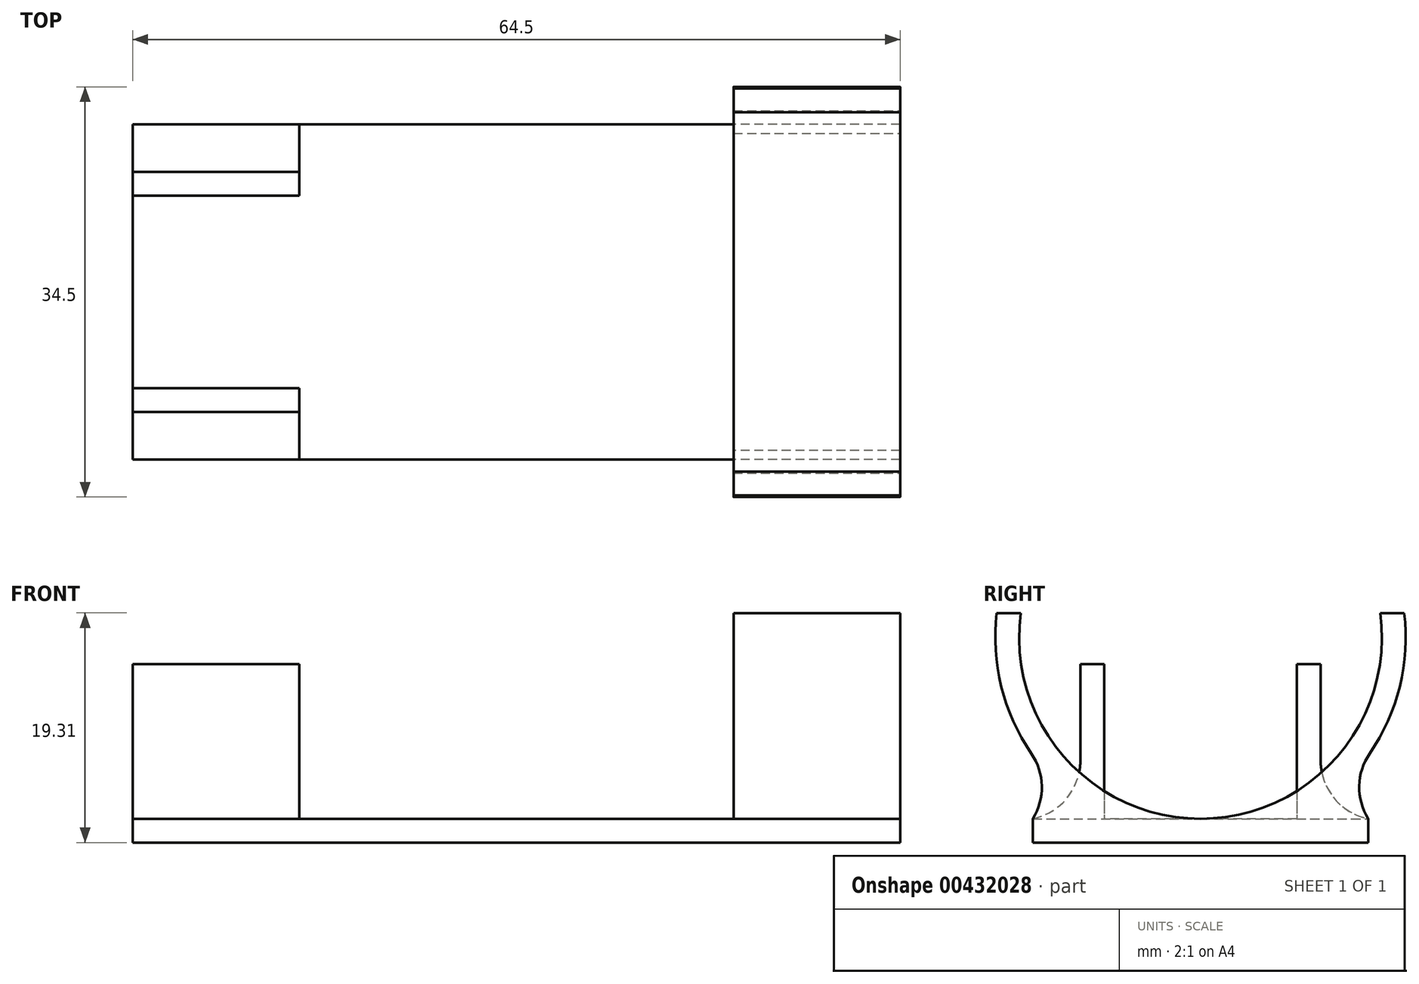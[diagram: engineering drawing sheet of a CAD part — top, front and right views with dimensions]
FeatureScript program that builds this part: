
annotation { "Feature Type Name" : "Feature", "Feature Type Description" : "" }
export const myFeature = defineFeature(function(context is Context, id is Id, definition is map)
    precondition{}
    {
        {
            var Q0;
            Q0=qCreatedBy(makeId("Right.planeOp"),FACE);
            var sketch = newSketch(context, id + "F0", { "sketchPlane" : qUnion([Q0])});
            skLineSegment(sketch, "E0", {"start": v(0, 0) * mm, "end": v(-10.1, 0) * mm});
            skLineSegment(sketch, "E1", {"start": v(-10.1, 0) * mm, "end": v(-10.1, 15) * mm});
            skLineSegment(sketch, "E2", {"start": v(-10.1, 15) * mm, "end": v(-8.1, 15) * mm});
            skLineSegment(sketch, "E3", {"start": v(-8.1, 15) * mm, "end": v(-8.1, 2) * mm});
            skLineSegment(sketch, "E4", {"start": v(-8.1, 2) * mm, "end": v(0, 2) * mm});
            skLineSegment(sketch, "E5.MirrorCS", {"start": v(10.1, 15) * mm, "end": v(8.1, 15) * mm});
            skLineSegment(sketch, "E6.MirrorCS", {"start": v(0, 0) * mm, "end": v(10.1, 0) * mm});
            skLineSegment(sketch, "E7.MirrorCS", {"start": v(8.1, 2) * mm, "end": v(0, 2) * mm});
            skLineSegment(sketch, "E8.MirrorCS", {"start": v(10.1, 0) * mm, "end": v(10.1, 15) * mm});
            skLineSegment(sketch, "E9.MirrorCS", {"start": v(8.1, 15) * mm, "end": v(8.1, 2) * mm});
            skLineSegment(sketch, "E10", {"start": v(-8.1, 2) * mm, "end": v(-10.1, 2) * mm});
            skLineSegment(sketch, "E11", {"start": v(8.1, 2) * mm, "end": v(10.1, 2) * mm});
            skLineSegment(sketch, "E12.bottom", {"start": v(-10.1, 2) * mm, "end": v(-14.1, 2) * mm});
            skLineSegment(sketch, "E12.top", {"start": v(-10.1, 0) * mm, "end": v(-14.1, 0) * mm});
            skLineSegment(sketch, "E12.left", {"start": v(-10.1, 2) * mm, "end": v(-10.1, 0) * mm});
            skLineSegment(sketch, "E12.right", {"start": v(-14.1, 2) * mm, "end": v(-14.1, 0) * mm});
            skLineSegment(sketch, "E13.MirrorCS", {"start": v(10.1, 0) * mm, "end": v(14.1, 0) * mm});
            skLineSegment(sketch, "E14.MirrorCS", {"start": v(14.1, 2) * mm, "end": v(14.1, 0) * mm});
            skLineSegment(sketch, "E15.MirrorCS", {"start": v(10.1, 2) * mm, "end": v(14.1, 2) * mm});
            skSolve(sketch);
        }
        {
            var Q0;
            {var subQ2=sQuery(id+"F0.wireOp",EDGE,"E0");Q0=makeQuery(id+"F0.imprint","IMPRINT",FACE,{"disambiguationData":[TD([[makeQuery(id+"F0.imprint","IMPRINT",EDGE,{"derivedFrom":subQ2}),-1.0]])]});}
            var Q1;
            {var subQ2=sQuery(id+"F0.wireOp",EDGE,"E2");Q1=makeQuery(id+"F0.imprint","IMPRINT",FACE,{"disambiguationData":[TD([[makeQuery(id+"F0.imprint","IMPRINT",EDGE,{"derivedFrom":subQ2}),-1.0]])]});}
            var Q2;
            {var subQ0=sQuery(id+"F0.wireOp",EDGE,"E5.MirrorCS");Q2=makeQuery(id+"F0.imprint","IMPRINT",FACE,{"disambiguationData":[TD([[makeQuery(id+"F0.imprint","IMPRINT",EDGE,{"derivedFrom":subQ0}),1.0]])]});}
            var Q3;
            {var subQ2=sQuery(id+"F0.wireOp",EDGE,"E12.bottom");Q3=makeQuery(id+"F0.imprint","IMPRINT",FACE,{"disambiguationData":[TD([[makeQuery(id+"F0.imprint","IMPRINT",EDGE,{"derivedFrom":subQ2}),1.0]])]});}
            var Q4;
            {var subQ0=sQuery(id+"F0.wireOp",EDGE,"E13.MirrorCS");Q4=makeQuery(id+"F0.imprint","IMPRINT",FACE,{"disambiguationData":[TD([[makeQuery(id+"F0.imprint","IMPRINT",EDGE,{"derivedFrom":subQ0}),1.0]])]});}
            extrude(context, id + "F1", {"entities" : qUnion([Q0, Q1, Q2, Q3, Q4]), "depth" : 14 * mm, "offsetDistance" : 25 * mm});
        }
        {
            var Q0;
            {var subQ2=sQuery(id+"F0.wireOp",EDGE,"E12.bottom");Q0=makeQuery(id+"F0.imprint","IMPRINT",FACE,{"disambiguationData":[TD([[makeQuery(id+"F0.imprint","IMPRINT",EDGE,{"derivedFrom":subQ2}),1.0]])]});}
            var Q1;
            {var subQ2=sQuery(id+"F0.wireOp",EDGE,"E0");Q1=makeQuery(id+"F0.imprint","IMPRINT",FACE,{"disambiguationData":[TD([[makeQuery(id+"F0.imprint","IMPRINT",EDGE,{"derivedFrom":subQ2}),-1.0]])]});}
            var Q2;
            {var subQ0=sQuery(id+"F0.wireOp",EDGE,"E13.MirrorCS");Q2=makeQuery(id+"F0.imprint","IMPRINT",FACE,{"disambiguationData":[TD([[makeQuery(id+"F0.imprint","IMPRINT",EDGE,{"derivedFrom":subQ0}),1.0]])]});}
            extrude(context, id + "F2", {"entities" : qUnion([Q0, Q1, Q2]), "operationType" : NewBodyOperationType.ADD, "depth" : 64.5 * mm, "offsetDistance" : 25 * mm});
        }
        {
            var Q0;
            Q0=makeQuery(id+"F2.opExtrude","CAP_FACE",FACE,{"disambiguationData":[OSD([sQuery(id+"F0.wireOp",EDGE,"E0"),sQuery(id+"F0.wireOp",EDGE,"E4"),sQuery(id+"F0.wireOp",EDGE,"E6.MirrorCS"),sQuery(id+"F0.wireOp",EDGE,"E7.MirrorCS"),sQuery(id+"F0.wireOp",EDGE,"E10"),sQuery(id+"F0.wireOp",EDGE,"E11"),sQuery(id+"F0.wireOp",EDGE,"E12.bottom"),sQuery(id+"F0.wireOp",EDGE,"E12.top"),sQuery(id+"F0.wireOp",EDGE,"E12.right"),sQuery(id+"F0.wireOp",EDGE,"E13.MirrorCS"),sQuery(id+"F0.wireOp",EDGE,"E14.MirrorCS"),sQuery(id+"F0.wireOp",EDGE,"E15.MirrorCS")])],"isStart":false});
            var sketch = newSketch(context, id + "F3", { "sketchPlane" : qUnion([Q0])});
            skLineSegment(sketch, "E16", {"start": v(0, 2) * mm, "end": v(0, 32.5) * mm, "construction": true});
            skPoint(sketch, "E16.endSnap0", {"position": v(0, 2) * mm});
            skArc(sketch, "E17", {"start": v(-15.11, 19.3) * mm, "mid": v(0, 2) * mm, "end": v(15.11, 19.3) * mm});
            skArc(sketch, "E18.0", {"start": v(-17.13, 19.3) * mm, "mid": v(0, 0) * mm, "end": v(17.13, 19.3) * mm});
            skLineSegment(sketch, "E19", {"start": v(-17.13, 19.3) * mm, "end": v(-15.11, 19.3) * mm});
            skLineSegment(sketch, "E20.trimOffspring", {"start": v(15.11, 19.3) * mm, "end": v(17.13, 19.3) * mm});
            skSolve(sketch);
        }
        {
            var Q0;
            Q0 = qSketchRegion(id + "F3", true);
            extrude(context, id + "F4", {"entities" : qUnion([Q0]), "operationType" : NewBodyOperationType.ADD, "oppositeDirection" : true, "depth" : 14 * mm, "offsetDistance" : 25 * mm});
        }
        {
            var Q0;
            Q0=makeQuery(id+"F1.opExtrude","SWEPT_EDGE",EDGE,{"disambiguationData":[OSD([sQuery(id+"F0.wireOp",EDGE,"E1"),sQuery(id+"F0.wireOp",EDGE,"E10"),sQuery(id+"F0.wireOp",EDGE,"E12.bottom")])]});
            var Q1;
            Q1=makeQuery(id+"F1.opExtrude","SWEPT_EDGE",EDGE,{"disambiguationData":[OSD([sQuery(id+"F0.wireOp",EDGE,"E8.MirrorCS"),sQuery(id+"F0.wireOp",EDGE,"E11"),sQuery(id+"F0.wireOp",EDGE,"E15.MirrorCS")])]});
            var Q2;
            {var subQ0=sQuery(id+"F0.wireOp",EDGE,"E15.MirrorCS");var subQ1=sQuery(id+"F0.wireOp",EDGE,"E12.bottom");var subQ2=sQuery(id+"F0.wireOp",EDGE,"E7.MirrorCS");var subQ3=sQuery(id+"F0.wireOp",EDGE,"E4");Q2=makeQuery(id+"F4.boolean.opBoolean","INTERSECT",EDGE,{"disambiguationData":[OD(0.0)],"derivedFrom":[makeQuery(id+"F2.boolean.opBoolean","MERGE",FACE,{"derivedFrom":[makeQuery(id+"F1.opExtrude","SWEPT_FACE",FACE,{"disambiguationData":[OSD([subQ3,subQ2])]}),makeQuery(id+"F1.opExtrude","SWEPT_FACE",FACE,{"disambiguationData":[OSD([subQ1])]}),makeQuery(id+"F1.opExtrude","SWEPT_FACE",FACE,{"disambiguationData":[OSD([subQ0])]}),makeQuery(id+"F2.opExtrude","SWEPT_FACE",FACE,{"disambiguationData":[OSD([subQ3,subQ2,sQuery(id+"F0.wireOp",EDGE,"E10"),sQuery(id+"F0.wireOp",EDGE,"E11"),subQ1,subQ0])]})]}),makeQuery(id+"F4.opExtrude","SWEPT_FACE",FACE,{"disambiguationData":[OSD([sQuery(id+"F3.wireOp",EDGE,"E18.0")])]})]});}
            var Q3;
            {var subQ0=sQuery(id+"F0.wireOp",EDGE,"E15.MirrorCS");var subQ1=sQuery(id+"F0.wireOp",EDGE,"E12.bottom");var subQ2=sQuery(id+"F0.wireOp",EDGE,"E7.MirrorCS");var subQ3=sQuery(id+"F0.wireOp",EDGE,"E4");Q3=makeQuery(id+"F4.boolean.opBoolean","INTERSECT",EDGE,{"disambiguationData":[OD(1.0)],"derivedFrom":[makeQuery(id+"F2.boolean.opBoolean","MERGE",FACE,{"derivedFrom":[makeQuery(id+"F1.opExtrude","SWEPT_FACE",FACE,{"disambiguationData":[OSD([subQ3,subQ2])]}),makeQuery(id+"F1.opExtrude","SWEPT_FACE",FACE,{"disambiguationData":[OSD([subQ1])]}),makeQuery(id+"F1.opExtrude","SWEPT_FACE",FACE,{"disambiguationData":[OSD([subQ0])]}),makeQuery(id+"F2.opExtrude","SWEPT_FACE",FACE,{"disambiguationData":[OSD([subQ3,subQ2,sQuery(id+"F0.wireOp",EDGE,"E10"),sQuery(id+"F0.wireOp",EDGE,"E11"),subQ1,subQ0])]})]}),makeQuery(id+"F4.opExtrude","SWEPT_FACE",FACE,{"disambiguationData":[OSD([sQuery(id+"F3.wireOp",EDGE,"E18.0")])]})]});}
            fillet(context, id + "F5", {"entities" : qUnion([Q0, Q1, Q2, Q3]), "radius" : 5 * mm, "tangentPropagation" : true, "allowEdgeOverflow" : false});
        }
    });
